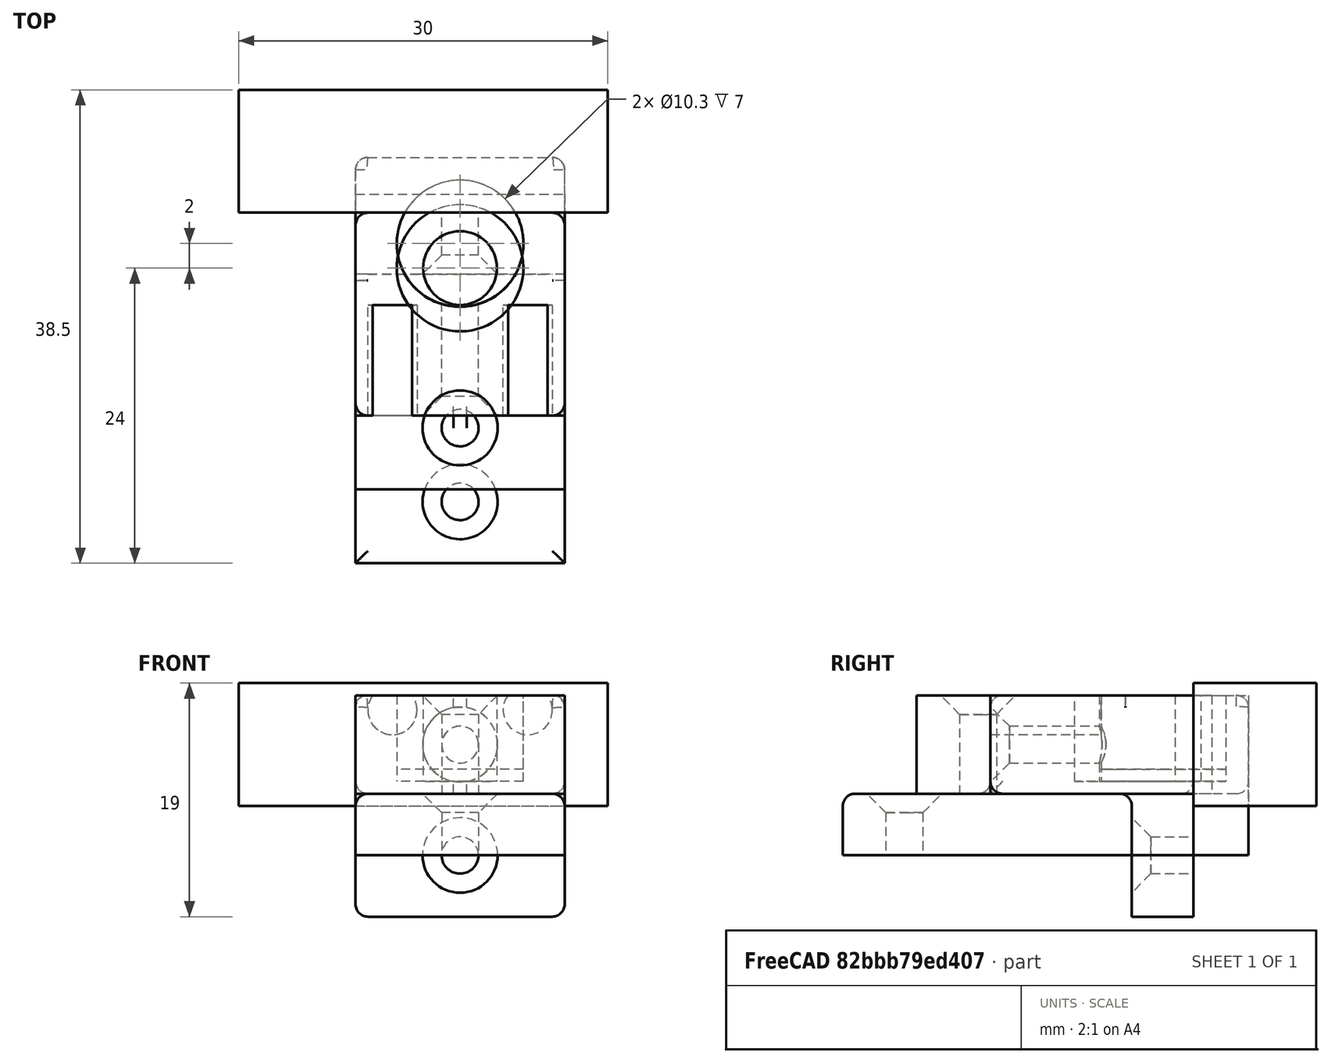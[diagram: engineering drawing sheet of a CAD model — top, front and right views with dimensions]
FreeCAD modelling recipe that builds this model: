
FCSTD DOCUMENT  (FreeCAD 0.20R29603 (Git))
Label: soportes
License: All rights reserved
LicenseURL: http://en.wikipedia.org/wiki/All_rights_reserved
objects: Part::Box×13, Part::Fillet×13, Part::Cut×12, Sketcher::SketchObject×9, Part::MultiFuse×8, Part::Cylinder×7, PartDesign::Hole×5, Part::Feature×5, PartDesign::Pad×3, PartDesign::Body×3, Mesh::Feature×3, PartDesign::Pocket×1
note: 88 computed .brp shape members not serialized (recipe doc carries the construction recipe); baked Part::Feature solids carry a one-line shape summary decoded from their .brp

FEATURE [Sketcher::SketchObject] Sketch
  FullyConstrained = true
  MapMode = 5
  Placement = pos=(0,0,0) rot=(1,0,0;1.5708rad)
  Support = -> [XZ_Plane]
  sketch-geometry (4):
    g0: LineSegment StartX=-8.5 StartY=4 StartZ=0 EndX=8.5 EndY=4 EndZ=0
    g1: LineSegment StartX=8.5 StartY=4 StartZ=0 EndX=8.5 EndY=-4 EndZ=0
    g2: LineSegment StartX=8.5 StartY=-4 StartZ=0 EndX=-8.5 EndY=-4 EndZ=0
    g3: LineSegment StartX=-8.5 StartY=-4 StartZ=0 EndX=-8.5 EndY=4 EndZ=0
  constraints (11):
    c: Coincident(g0,g1)
    c: Coincident(g1,g2)
    c: Coincident(g2,g3)
    c: Coincident(g3,g0)
    c: Horizontal(g0)
    c: Horizontal(g2)
    c: Vertical(g1)
    c: Vertical(g3)
    c: DistanceX(g0,g0) = 17
    c: Symmetric(g2,g0,g-1)
    c: DistanceY(g1,g1) = 8
FEATURE [PartDesign::Pad] Pad
  Direction = (0,-1,2e-16)
  Length = 18
  Length2 = 10
  Placement = pos=(0,0,0) rot=(1,0,0;1.5708rad)
  Profile = -> Sketch
  ReferenceAxis = -> Sketch [N_Axis]
  Type = 0
FEATURE [Sketcher::SketchObject] Sketch001
  FullyConstrained = false
  MapMode = 5
  Placement = pos=(0,-18,8e-15) rot=(1,0,0;1.5708rad)
  Support = -> [Pad]
  sketch-geometry (1):
    g0: Circle CenterX=0 CenterY=0 CenterZ=0 NormalX=0 NormalY=0 NormalZ=1 AngleXU=0 Radius=1.31488
  constraints (1):
    c: Coincident(g0,g-1)
FEATURE [PartDesign::Hole] Hole
  BaseFeature = -> Pad
  CustomThreadClearance = 0
  Depth = 10
  DepthType = 0
  Diameter = 3
  DrillForDepth = false
  DrillPoint = 1
  DrillPointAngle = 118
  HoleCutCountersinkAngle = 90
  HoleCutCustomValues = false
  HoleCutDepth = 0
  HoleCutDiameter = 6.1
  HoleCutType = 2
  ModelThread = false
  Placement = pos=(0,0,0) rot=(1,0,0;1.5708rad)
  Profile = -> Sketch001
  Tapered = false
  TaperedAngle = 90
  ThreadClass = 0
  ThreadDepth = 10
  ThreadDepthType = 0
  ThreadDirection = 0
  ThreadFit = 0
  ThreadSize = 0
  ThreadType = 0
  Threaded = false
  UseCustomThreadClearance = false
FEATURE [Sketcher::SketchObject] Sketch002
  FullyConstrained = true
  MapMode = 5
  Placement = pos=(0,2.6e-15,4) rot=(0,0,1;3.14159rad)
  Support = -> [Hole]
  sketch-geometry (1):
    g0: Circle CenterX=0 CenterY=6 CenterZ=0 NormalX=0 NormalY=0 NormalZ=1 AngleXU=0 Radius=5.15
  constraints (3):
    c: DistanceX(g0,g-1) = 0
    c: Diameter(g0) = 10.3
    c: DistanceY(g-1,g0) = 6
FEATURE [PartDesign::Hole] Hole001
  BaseFeature = -> Hole
  CustomThreadClearance = 0
  Depth = 7
  DepthType = 0
  Diameter = 6
  DrillForDepth = false
  DrillPoint = 0
  DrillPointAngle = 118
  HoleCutCountersinkAngle = 90
  HoleCutCustomValues = false
  HoleCutDepth = 0
  HoleCutDiameter = 6.1
  HoleCutType = 0
  ModelThread = false
  Placement = pos=(0,0,0) rot=(1,0,0;1.5708rad)
  Profile = -> Sketch002
  Tapered = false
  TaperedAngle = 90
  ThreadClass = 0
  ThreadDepth = 7
  ThreadDepthType = 0
  ThreadDirection = 0
  ThreadFit = 0
  ThreadSize = 0
  ThreadType = 0
  Threaded = false
  UseCustomThreadClearance = false
FEATURE [PartDesign::Body] Body
  Group = -> [Sketch,Pad,Sketch001,Hole,Sketch002,Hole001]
  Origin = -> Origin
  Tip = -> Hole001
FEATURE [Part::Cylinder] Cylinder
  Angle = 360
  AttacherType = Attacher::AttachEngine3D
  FirstAngle = 0
  Height = 10
  Placement = pos=(-5.5,-9,2.8) rot=(1,0,0;1.5708rad)
  Radius = 2
  SecondAngle = 0
FEATURE [Part::Cylinder] Cylinder001
  Angle = 360
  AttacherType = Attacher::AttachEngine3D
  FirstAngle = 0
  Height = 10
  Placement = pos=(5.5,-9,2.8) rot=(1,0,0;1.5708rad)
  Radius = 2
  SecondAngle = 0
FEATURE [Part::Cut] Cut
  Base = -> Body
  Tool = -> Cylinder
FEATURE [Part::Cut] Cut001
  Base = -> Cut
  Tool = -> Cylinder001
FEATURE [Part::Box] Box  label="Cube"
  AttacherType = Attacher::AttachEngine3D
  Height = 10
  Length = 30
  Placement = pos=(-18,-1.5,-5) rot=(0,0,1;0rad)
  Width = 10
FEATURE [Part::Cut] Cut002  label="Soporte Externo"
  Base = -> Cut001
  Tool = -> Box
FEATURE [Sketcher::SketchObject] Sketch003
  FullyConstrained = true
  MapMode = 5
  Placement = pos=(0,0,0) rot=(1,0,0;1.5708rad)
  Support = -> [XZ_Plane001]
  sketch-geometry (4):
    g0: LineSegment StartX=-8.5 StartY=4 StartZ=0 EndX=8.5 EndY=4 EndZ=0
    g1: LineSegment StartX=8.5 StartY=4 StartZ=0 EndX=8.5 EndY=-4 EndZ=0
    g2: LineSegment StartX=8.5 StartY=-4 StartZ=0 EndX=-8.5 EndY=-4 EndZ=0
    g3: LineSegment StartX=-8.5 StartY=-4 StartZ=0 EndX=-8.5 EndY=4 EndZ=0
  constraints (11):
    c: Coincident(g0,g1)
    c: Coincident(g1,g2)
    c: Coincident(g2,g3)
    c: Coincident(g3,g0)
    c: Horizontal(g0)
    c: Horizontal(g2)
    c: Vertical(g1)
    c: Vertical(g3)
    c: DistanceX(g0,g0) = 17
    c: Symmetric(g2,g0,g-1)
    c: DistanceY(g1,g1) = 8
FEATURE [PartDesign::Pad] Pad001
  Direction = (0,-1,-2e-16)
  Length = 24
  Length2 = 10
  Placement = pos=(0,0,0) rot=(1,0,0;1.5708rad)
  Profile = -> Sketch003
  ReferenceAxis = -> Sketch003 [N_Axis]
  Type = 0
FEATURE [Sketcher::SketchObject] Sketch005
  FullyConstrained = true
  MapMode = 5
  Placement = pos=(0,3e-15,4) rot=(0,0,1;3.14159rad)
  sketch-geometry (1):
    g0: Circle CenterX=0 CenterY=6 CenterZ=0 NormalX=0 NormalY=0 NormalZ=1 AngleXU=0 Radius=5.15
  constraints (3):
    c: DistanceX(g0,g-1) = 0
    c: Diameter(g0) = 10.3
    c: DistanceY(g-1,g0) = 6
FEATURE [PartDesign::Pocket] Pocket
  BaseFeature = -> Pad001
  Direction = (0,-7e-16,-1)
  Length = 7
  Length2 = 5
  Placement = pos=(0,0,0) rot=(1,0,0;1.5708rad)
  Profile = -> Sketch005
  ReferenceAxis = -> Sketch005 [N_Axis]
  Type = 0
FEATURE [Sketcher::SketchObject] Sketch006
  FullyConstrained = true
  MapMode = 5
  Placement = pos=(0,9e-16,4) rot=(0,0,1;3.14159rad)
  Support = -> [Pocket]
  sketch-geometry (1):
    g0: Circle CenterX=0 CenterY=19 CenterZ=0 NormalX=0 NormalY=0 NormalZ=1 AngleXU=0 Radius=3.05
  constraints (3):
    c: PointOnObject(g0,g-2)
    c: Diameter(g0) = 6.1
    c: DistanceY(g-1,g0) = 19
FEATURE [PartDesign::Hole] Hole002
  BaseFeature = -> Pocket
  CustomThreadClearance = 0
  Depth = 25
  DepthType = 0
  Diameter = 3
  DrillForDepth = false
  DrillPoint = 1
  DrillPointAngle = 118
  HoleCutCountersinkAngle = 90
  HoleCutCustomValues = false
  HoleCutDepth = 0
  HoleCutDiameter = 6.1
  HoleCutType = 2
  ModelThread = false
  Placement = pos=(0,0,0) rot=(1,0,0;1.5708rad)
  Profile = -> Sketch006
  Tapered = false
  TaperedAngle = 90
  ThreadClass = 0
  ThreadDepth = 25
  ThreadDepthType = 0
  ThreadDirection = 0
  ThreadFit = 0
  ThreadSize = 0
  ThreadType = 0
  Threaded = false
  UseCustomThreadClearance = false
FEATURE [PartDesign::Body] Body001  label="mal_Sopoprte_arriba"
  Group = -> [Sketch003,Pad001,Sketch005,Pocket,Sketch006,Hole002]
  Origin = -> Origin001
  Tip = -> Hole002
FEATURE [Part::Feature] Cut002001  label="Soporte Externo001"
  shape: bbox 17 x 16.5 x 8 mm, 16 faces (baked)
FEATURE [Part::Box] Box001  label="Cube001"
  AttacherType = Attacher::AttachEngine3D
  Height = 8
  Length = 6.5
  Placement = pos=(-3.3,-18,-4) rot=(0,0,1;0rad)
  Width = 16
FEATURE [Part::MultiFuse] Fusion
  Shapes = -> [Cut002001,Box001]
FEATURE [Part::Feature] Body001001  label="Sopoprte_arriba001"
  shape: bbox 17 x 24 x 8 mm, 10 faces (baked)
FEATURE [Part::Box] Box003  label="Cube003"
  AttacherType = Attacher::AttachEngine3D
  Height = 20
  Length = 26
  Placement = pos=(-14,-14,-9) rot=(0,0,1;0rad)
  Width = 23
FEATURE [Part::Cut] Cut002002
  Base = -> Body001001
  Tool = -> Box003
FEATURE [Part::Box] Box004  label="Cube004"
  AttacherType = Attacher::AttachEngine3D
  Height = 10
  Length = 33
  Placement = pos=(-16,-24,-11) rot=(0,0,1;0rad)
  Width = 10
FEATURE [Part::Cut] Cut002003
  Base = -> Cut002002
  Placement = pos=(0,-2.5,10) rot=(1,0,0;1.5708rad)
  Tool = -> Box004
FEATURE [Part::MultiFuse] Fusion001
  Shapes = -> [Cut002003,Fusion]
FEATURE [Part::Fillet] Fillet
  Base = -> Fusion001
  Edges = 2 edges r=1: [Edge16,Edge18]
FEATURE [Part::Fillet] Fillet001
  Base = -> Fillet
  Edges = 3 edges r=1: [Edge16,Edge21,Edge25]
FEATURE [Part::Fillet] Fillet002  label="soporte_pared_3"
  Base = -> Fillet001
  Edges = 3 edges r=1: [Edge2,Edge9,Edge14]
FEATURE [Part::Box] Box005  label="Cube005"
  AttacherType = Attacher::AttachEngine3D
  Height = 10
  Length = 30
  Placement = pos=(-18,-1.5,-5) rot=(0,0,1;0rad)
  Width = 10
FEATURE [Part::Cylinder] Cylinder002
  Angle = 360
  AttacherType = Attacher::AttachEngine3D
  FirstAngle = 0
  Height = 10
  Placement = pos=(-5.5,-9,2.8) rot=(1,0,0;1.5708rad)
  Radius = 2
  SecondAngle = 0
FEATURE [Part::Cylinder] Cylinder003
  Angle = 360
  AttacherType = Attacher::AttachEngine3D
  FirstAngle = 0
  Height = 10
  Placement = pos=(5.5,-9,2.8) rot=(1,0,0;1.5708rad)
  Radius = 2
  SecondAngle = 0
FEATURE [Sketcher::SketchObject] Sketch007
  FullyConstrained = true
  MapMode = 5
  Placement = pos=(0,0,0) rot=(1,0,0;1.5708rad)
  Support = -> [XZ_Plane002]
  sketch-geometry (4):
    g0: LineSegment StartX=-8.5 StartY=4 StartZ=0 EndX=8.5 EndY=4 EndZ=0
    g1: LineSegment StartX=8.5 StartY=4 StartZ=0 EndX=8.5 EndY=-4 EndZ=0
    g2: LineSegment StartX=8.5 StartY=-4 StartZ=0 EndX=-8.5 EndY=-4 EndZ=0
    g3: LineSegment StartX=-8.5 StartY=-4 StartZ=0 EndX=-8.5 EndY=4 EndZ=0
  constraints (11):
    c: Coincident(g0,g1)
    c: Coincident(g1,g2)
    c: Coincident(g2,g3)
    c: Coincident(g3,g0)
    c: Horizontal(g0)
    c: Horizontal(g2)
    c: Vertical(g1)
    c: Vertical(g3)
    c: DistanceX(g0,g0) = 17
    c: Symmetric(g2,g0,g-1)
    c: DistanceY(g1,g1) = 8
FEATURE [PartDesign::Pad] Pad002
  Direction = (0,-1,2e-16)
  Length = 18
  Length2 = 10
  Placement = pos=(0,0,0) rot=(1,0,0;1.5708rad)
  Profile = -> Sketch007
  ReferenceAxis = -> Sketch007 [N_Axis]
  Type = 0
FEATURE [Sketcher::SketchObject] Sketch008
  FullyConstrained = false
  MapMode = 5
  Placement = pos=(0,-18,8e-15) rot=(1,0,0;1.5708rad)
  Support = -> [Pad002]
  sketch-geometry (1):
    g0: Circle CenterX=0 CenterY=0 CenterZ=0 NormalX=0 NormalY=0 NormalZ=1 AngleXU=0 Radius=1.31488
  constraints (1):
    c: Coincident(g0,g-1)
FEATURE [PartDesign::Hole] Hole003
  BaseFeature = -> Pad002
  CustomThreadClearance = 0
  Depth = 10
  DepthType = 0
  Diameter = 3
  DrillForDepth = false
  DrillPoint = 1
  DrillPointAngle = 118
  HoleCutCountersinkAngle = 90
  HoleCutCustomValues = false
  HoleCutDepth = 0
  HoleCutDiameter = 6.1
  HoleCutType = 2
  ModelThread = false
  Placement = pos=(0,0,0) rot=(1,0,0;1.5708rad)
  Profile = -> Sketch008
  Tapered = false
  TaperedAngle = 90
  ThreadClass = 0
  ThreadDepth = 10
  ThreadDepthType = 0
  ThreadDirection = 0
  ThreadFit = 0
  ThreadSize = 0
  ThreadType = 0
  Threaded = false
  UseCustomThreadClearance = false
FEATURE [Sketcher::SketchObject] Sketch009
  FullyConstrained = true
  MapMode = 5
  Placement = pos=(0,2.6e-15,4) rot=(0,0,1;3.14159rad)
  Support = -> [Hole003]
  sketch-geometry (1):
    g0: Circle CenterX=0 CenterY=6 CenterZ=0 NormalX=0 NormalY=0 NormalZ=1 AngleXU=0 Radius=5.15
  constraints (3):
    c: DistanceX(g0,g-1) = 0
    c: Diameter(g0) = 10.3
    c: DistanceY(g-1,g0) = 6
FEATURE [PartDesign::Hole] Hole004
  BaseFeature = -> Hole003
  CustomThreadClearance = 0
  Depth = 7
  DepthType = 0
  Diameter = 6
  DrillForDepth = false
  DrillPoint = 0
  DrillPointAngle = 118
  HoleCutCountersinkAngle = 90
  HoleCutCustomValues = false
  HoleCutDepth = 0
  HoleCutDiameter = 6.1
  HoleCutType = 0
  ModelThread = false
  Placement = pos=(0,0,0) rot=(1,0,0;1.5708rad)
  Profile = -> Sketch009
  Tapered = false
  TaperedAngle = 90
  ThreadClass = 0
  ThreadDepth = 7
  ThreadDepthType = 0
  ThreadDirection = 0
  ThreadFit = 0
  ThreadSize = 0
  ThreadType = 0
  Threaded = false
  UseCustomThreadClearance = false
FEATURE [PartDesign::Body] Body001002
  Group = -> [Sketch007,Pad002,Sketch008,Hole003,Sketch009,Hole004]
  Origin = -> Origin002
  Tip = -> Hole004
FEATURE [Part::Cut] Cut002004
  Base = -> Body001002
  Tool = -> Cylinder002
FEATURE [Part::Feature] Cut002004001
  shape: bbox 17 x 18 x 8 mm, 13 faces (baked)
FEATURE [Part::Cylinder] Cylinder004
  Angle = 360
  AttacherType = Attacher::AttachEngine3D
  FirstAngle = 0
  Height = 10
  Placement = pos=(-5.5,-9,2.8) rot=(1,0,0;1.5708rad)
  Radius = 2
  SecondAngle = 0
FEATURE [Part::MultiFuse] Fusion002
  Shapes = -> [Cylinder004,Cut002004001,Cylinder003]
FEATURE [Part::Box] Box006  label="Cube006"
  AttacherType = Attacher::AttachEngine3D
  Height = 10
  Length = 18
  Placement = pos=(-9,-20,4) rot=(0,0,1;0rad)
  Width = 12
FEATURE [Part::Box] Box007  label="Cube007"
  AttacherType = Attacher::AttachEngine3D
  Height = 10
  Length = 18
  Placement = pos=(-9,-30,-1) rot=(0,0,1;0rad)
  Width = 12
FEATURE [Part::Cut] Cut002004002
  Base = -> Fusion002
  Tool = -> Box006
FEATURE [Part::Cut] Cut002004003
  Base = -> Cut002004002
  Tool = -> Box007
FEATURE [Part::Feature] Body001003  label="Sopoprte_arriba002"
  Placement = pos=(0,-6,-8) rot=(0,0,1;0rad)
  shape: bbox 17 x 24 x 8 mm, 10 faces (baked)
FEATURE [Part::MultiFuse] Fusion003
  Shapes = -> [Body001003,Cut002004003]
FEATURE [Part::Box] Box008  label="Cube008"
  AttacherType = Attacher::AttachEngine3D
  Height = 10
  Length = 17
  Placement = pos=(-8.5,-10,-12) rot=(0,0,1;0rad)
  Width = 10
FEATURE [Part::MultiFuse] Fusion004
  Shapes = -> [Fusion003,Box008]
FEATURE [Part::Box] Box009  label="Cube009"
  AttacherType = Attacher::AttachEngine3D
  Height = 3
  Length = 77
  Placement = pos=(-39,-30,-12) rot=(0,0,1;0rad)
  Width = 32
FEATURE [Part::Cut] Cut002004004
  Base = -> Fusion004
  Tool = -> Box009
FEATURE [Part::Fillet] Fillet003
  Base = -> Cut002004004
  Edges = 1 edges r=1: [Edge42]
FEATURE [Part::Fillet] Fillet004
  Base = -> Fillet003
  Edges = 5 edges r=1: [Edge48,Edge51,Edge54,Edge96,Edge97]
FEATURE [Part::Fillet] Fillet005  label="soprte_arriba_31"
  Base = -> Fillet004
  Edges = 16 edges r=1: [Edge1,Edge2,Edge3,Edge4,Edge5,Edge11,Edge15,Edge33,Edge36,Edge52,Edge62,Edge63,Edge68,Edge69,Edge100,Edge101]
FEATURE [Part::Feature] Cut002004005  label="Soporte Externo002"
  shape: bbox 17 x 16.5 x 8 mm, 16 faces (baked)
FEATURE [Part::Fillet] Fillet006  label="soporte_externo_3"
  Base = -> Cut002004005
  Edges = 7 edges r=1: [Edge14,Edge15,Edge16,Edge17,Edge18,Edge24,Edge32]
FEATURE [Part::Box] Box010  label="Cube010"
  AttacherType = Attacher::AttachEngine3D
  Height = 5
  Length = 12
  Placement = pos=(-6,-18,-9) rot=(0,0,1;0rad)
  Width = 9
FEATURE [Part::MultiFuse] Fusion005  label="soprte_arriba_3"
  Shapes = -> [Fillet005,Box010]
FEATURE [Part::Cylinder] Cylinder005
  Angle = 360
  AttacherType = Attacher::AttachEngine3D
  FirstAngle = 0
  Height = 6
  Placement = pos=(0,-4,-2) rot=(0,0,1;0rad)
  Radius = 5.15
  SecondAngle = 0
FEATURE [Part::Cylinder] Cylinder006
  Angle = 360
  AttacherType = Attacher::AttachEngine3D
  FirstAngle = 0
  Height = 7
  Placement = pos=(0,-4,-3) rot=(0,0,1;0rad)
  Radius = 5.15
  SecondAngle = 0
FEATURE [Part::Box] Box011  label="Cube011"
  AttacherType = Attacher::AttachEngine3D
  Height = 13
  Length = 17
  Placement = pos=(-8.5,-7,-9) rot=(0,0,1;0rad)
  Width = 10
FEATURE [Part::Box] Box012  label="Cube012"
  AttacherType = Attacher::AttachEngine3D
  Height = 13
  Length = 17
  Placement = pos=(-8.5,-7,-9) rot=(0,0,1;0rad)
  Width = 10
FEATURE [Part::MultiFuse] Fusion006
  Shapes = -> [Fusion005,Box011]
FEATURE [Part::Cut] Cut002004006
  Base = -> Fusion006
  Tool = -> Cylinder005
FEATURE [Part::Fillet] Fillet007
  Base = -> Cut002004006
  Edges = 2 edges r=0.9: [Edge38,Edge46]
FEATURE [Part::Fillet] Fillet008  label="soprte_arriba_4"
  Base = -> Fillet007
  Edges = 1 edges r=1: [Edge18]
FEATURE [Part::MultiFuse] Fusion007
  Shapes = -> [Cut002,Box012]
FEATURE [Part::Cut] Cut002004007
  Base = -> Fusion007
  Tool = -> Cylinder006
FEATURE [Part::Fillet] Fillet009
  Base = -> Cut002004007
  Edges = 5 edges r=1: [Edge6,Edge9,Edge17,Edge19,Edge23]
FEATURE [Part::Fillet] Fillet010  label="Soporte Externo_41"
  Base = -> Fillet009
  Edges = 1 edges r=1: [Edge9]
FEATURE [Mesh::Feature] Mesh  label="soporte_pared_3 (Meshed)"
FEATURE [Mesh::Feature] Mesh001  label="soprte_arriba_4 (Meshed)"
FEATURE [Part::Box] Box013  label="Cube013"
  AttacherType = Attacher::AttachEngine3D
  Height = 13
  Length = 17
  Placement = pos=(-8.5,-9,-17) rot=(0,0,1;0rad)
  Width = 12
FEATURE [Part::Cut] Cut002004008
  Base = -> Fillet010
  Tool = -> Box013
FEATURE [Part::Fillet] Fillet011
  Base = -> Cut002004008
  Edges = 10 edges r=1: [Edge3,Edge8,Edge12,Edge13,Edge14,Edge16,Edge17,Edge18,Edge56,Edge58]
FEATURE [Part::Fillet] Fillet012  label="Soporte Externo_4"
  Base = -> Fillet011
  Edges = 1 edges r=1: [Edge44]
FEATURE [Mesh::Feature] Mesh002  label="Soporte Externo_4 (Meshed)"
